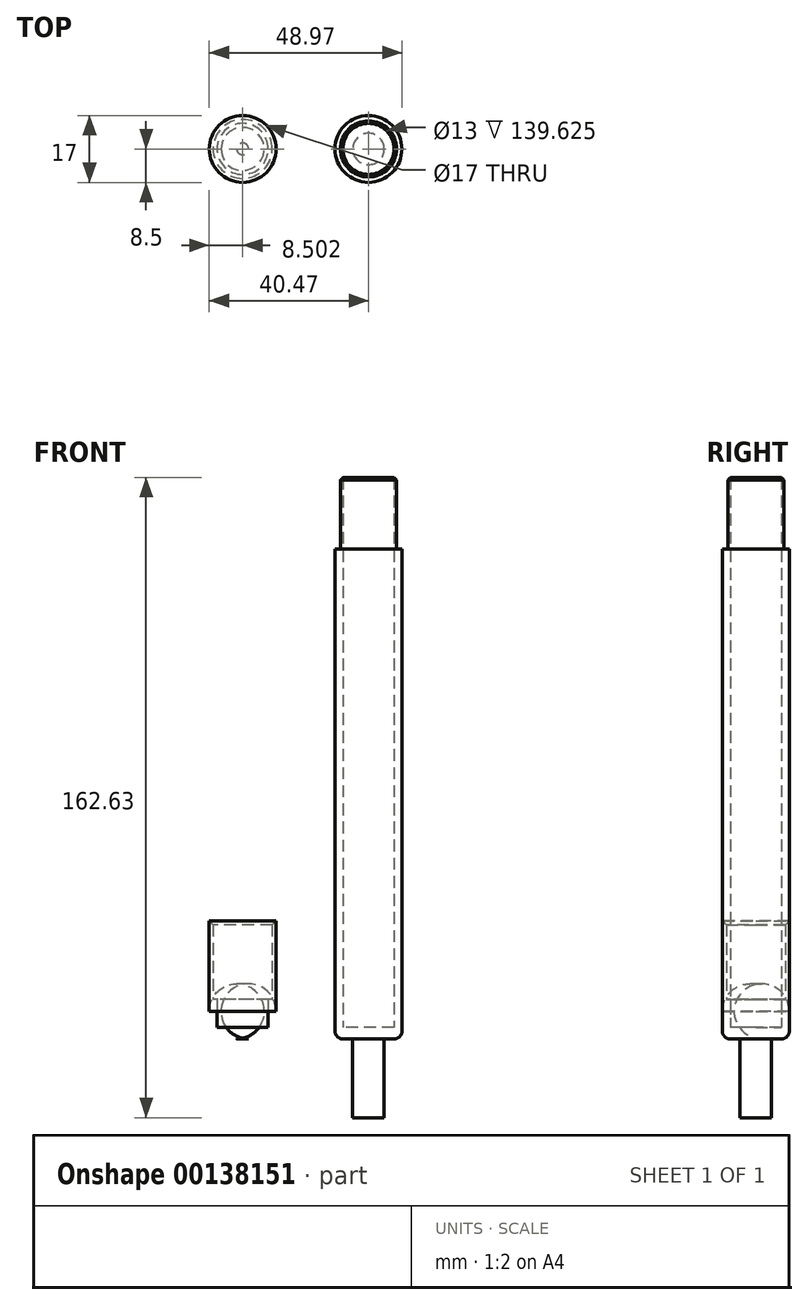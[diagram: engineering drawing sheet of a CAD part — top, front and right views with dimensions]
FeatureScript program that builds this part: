
annotation { "Feature Type Name" : "Feature", "Feature Type Description" : "" }
export const myFeature = defineFeature(function(context is Context, id is Id, definition is map)
    precondition{}
    {
        {
            var Q0;
            Q0=qCreatedBy(makeId("Top.planeOp"),FACE);
            var sketch = newSketch(context, id + "F0", { "sketchPlane" : qUnion([Q0])});
            skCircle(sketch, "E0", {"center": v(0, 0) * mm, "radius": 8.5 * mm});
            skCircle(sketch, "E1", {"center": v(0, 0) * mm, "radius": 6.5 * mm});
            skPoint(sketch, "E2", {"position": v(-31.97, 0) * mm});
            skCircle(sketch, "E3", {"center": v(-31.97, 0) * mm, "radius": 8.5 * mm});
            skCircle(sketch, "E4", {"center": v(-31.97, 0) * mm, "radius": 6.5 * mm});
            skCircle(sketch, "E5", {"center": v(-31.97, 0) * mm, "radius": 7.5 * mm});
            skCircle(sketch, "E6", {"center": v(0, 0) * mm, "radius": 7.12 * mm});
            skCircle(sketch, "E7", {"center": v(0, 0) * mm, "radius": 4 * mm});
            skSolve(sketch);
        }
        {
            var Q0;
            Q0=makeQuery(id+"F0.imprint","IMPRINT",FACE,{"disambiguationData":[TD([[makeQuery(id+"F0.imprint","IMPRINT",EDGE,{"derivedFrom":sQuery(id+"F0.wireOp",EDGE,"E1")}),1.0]])]});
            var Q1;
            Q1=makeQuery(id+"F0.imprint","IMPRINT",FACE,{"disambiguationData":[TD([[makeQuery(id+"F0.imprint","IMPRINT",EDGE,{"derivedFrom":sQuery(id+"F0.wireOp",EDGE,"E7")}),1.0]])]});
            var Q2;
            Q2=makeQuery(id+"F0.imprint","IMPRINT",FACE,{"disambiguationData":[TD([[makeQuery(id+"F0.imprint","IMPRINT",EDGE,{"derivedFrom":sQuery(id+"F0.wireOp",EDGE,"E4")}),1.0]])]});
            extrude(context, id + "F1", {"entities" : qUnion([Q0, Q1, Q2]), "depth" : 3 * mm});
        }
        {
            var Q0;
            Q0=makeQuery(id+"F0.imprint","IMPRINT",FACE,{"disambiguationData":[TD([[makeQuery(id+"F0.imprint","IMPRINT",EDGE,{"derivedFrom":sQuery(id+"F0.wireOp",EDGE,"E4")}),-1.0]])]});
            extrude(context, id + "F2", {"entities" : qUnion([Q0]), "operationType" : NewBodyOperationType.ADD, "depth" : 10 * mm});
        }
        {
            var Q0;
            Q0=makeQuery(id+"F0.imprint","IMPRINT",FACE,{"disambiguationData":[TD([[makeQuery(id+"F0.imprint","IMPRINT",EDGE,{"derivedFrom":sQuery(id+"F0.wireOp",EDGE,"E3")}),1.0]])]});
            extrude(context, id + "F3", {"entities" : qUnion([Q0]), "operationType" : NewBodyOperationType.ADD, "depth" : 30 * mm});
        }
        {
            var Q0;
            Q0=makeQuery(id+"F0.imprint","IMPRINT",FACE,{"disambiguationData":[TD([[makeQuery(id+"F0.imprint","IMPRINT",EDGE,{"derivedFrom":sQuery(id+"F0.wireOp",EDGE,"E1")}),-1.0]])]});
            extrude(context, id + "F4", {"entities" : qUnion([Q0]), "operationType" : NewBodyOperationType.ADD, "depth" : 143 * mm});
        }
        {
            var Q0;
            Q0=makeQuery(id+"F0.imprint","IMPRINT",FACE,{"disambiguationData":[TD([[makeQuery(id+"F0.imprint","IMPRINT",EDGE,{"derivedFrom":sQuery(id+"F0.wireOp",EDGE,"E0")}),1.0]])]});
            extrude(context, id + "F5", {"entities" : qUnion([Q0]), "operationType" : NewBodyOperationType.ADD, "depth" : 124.5 * mm});
        }
        {
            var Q0;
            Q0=makeQuery(id+"F3.opExtrude","CAP_EDGE",EDGE,{"disambiguationData":[OSD([sQuery(id+"F0.wireOp",EDGE,"E3")])],"isStart":true});
            fillet(context, id + "F6", {"entities" : qUnion([Q0]), "radius" : 7 * mm, "tangentPropagation" : true, "allowEdgeOverflow" : false});
        }
        {
            var Q0;
            Q0=makeQuery(id+"F5.opExtrude","CAP_EDGE",EDGE,{"disambiguationData":[OSD([sQuery(id+"F0.wireOp",EDGE,"E0")])],"isStart":true});
            fillet(context, id + "F7", {"entities" : qUnion([Q0]), "radius" : 2 * mm, "tangentPropagation" : true, "allowEdgeOverflow" : false});
        }
        {
            var Q0;
            Q0=makeQuery(id+"F4.opExtrude","CAP_EDGE",EDGE,{"disambiguationData":[OSD([sQuery(id+"F0.wireOp",EDGE,"E6")])],"isStart":false});
            var Q1;
            Q1=makeQuery(id+"F3.opExtrude","CAP_EDGE",EDGE,{"disambiguationData":[OSD([sQuery(id+"F0.wireOp",EDGE,"E5")])],"isStart":false});
            chamfer(context, id + "F8", {"entities" : qUnion([Q0, Q1]), "width" : 1 * mm, "tangentPropagation" : true});
        }
        {
            var Q0;
            Q0=makeQuery(id+"F0.imprint","IMPRINT",FACE,{"disambiguationData":[TD([[makeQuery(id+"F0.imprint","IMPRINT",EDGE,{"derivedFrom":sQuery(id+"F0.wireOp",EDGE,"E7")}),1.0]])]});
            extrude(context, id + "F9", {"entities" : qUnion([Q0]), "operationType" : NewBodyOperationType.ADD, "oppositeDirection" : true, "depth" : 20 * mm});
        }
    });
